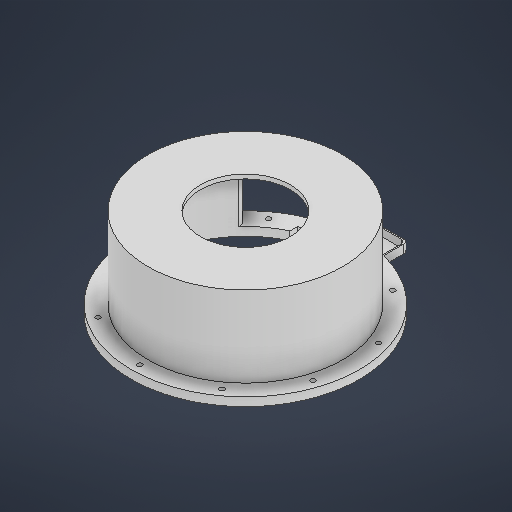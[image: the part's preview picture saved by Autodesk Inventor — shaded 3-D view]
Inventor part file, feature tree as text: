
AUTODESK INVENTOR PART (.ipt)
format: ipt  version: 2025 (Build 290162000, 162)  size: 350,208 bytes
history: native  units: in
note: dims shown in document units (in); Inventor stores cm internally (conversion verified against a paired STEP export)
features: extrude x8, sketch x5, fillet x2
ambient origin geometry x8: Origin, YZ Plane, XZ Plane, XY Plane, X Axis, Y Axis, Z Axis, Center Point
bodies: Solid1 (feature_tree)
feature tree (15):
  sketch  "Sketch1"  dims[d5=0.0in d7=0.0in]
  extrude  "Extrusion1"  TaperAngle=0.0deg  [1 undecoded]
  extrude  "Extrusion2"  Depth=4.5276in
  extrude  "Extrusion7"  Depth=2.5591in
  sketch  "Sketch24"  dims[d237=0.0591in d238=2.564in]
  extrude  "Extrusion30"  Depth=0.0591in
  extrude  "Extrusion31"  Depth=0.3937in
  extrude  "Extrusion32"  Depth=0.3937in
  extrude  "Extrusion35"  Depth=0.3937in
  fillet  "Fillet19"  Radius=1.5298in
  fillet  "Fillet20"  Radius=0.0787in
  extrude  "Extrusion36"  Depth=0.3937in
  sketch  "Sketch2"  dims[d18=0.0in d52=4.5276in]
  sketch  "Sketch27"  dims[d240=0.8253in d241=10.6299in d242=2.7608in d243=0.5433in d244=1.5298in d247=0.0787in d248=3.5433in d249=3.6614in d250=0.0in d251=3.6614in d252=0.0in d253=9.4488in d254=0.3937in d255=0.0in d267=0.0394in d268=0.0in d274=0.1969in d275=0.0787in d276=9.8425in d277=0.2165in d278=3.937in d280=360.0deg d282=0.3937in d283=0.0in d113=0.0197in d114=0.0344in d115=0.0197in d116=0.0344in d167=0.0197in d168=0.0344in d169=0.0197in d170=0.0344in d215=0.0197in d216=0.0344in d217=0.0197in d218=0.0344in d219=0.0in d220=0.0in d256=0.0197in d257=0.0344in]
  sketch  "Sketch Circular Pattern6"  dims[d234=0.0787in d235=2.5591in]
note: 1 required parameter value undecoded (feature->parameter linkage not recoverable at this tier; creation-order binding heuristic only, values carry confidence <= 0.55)
